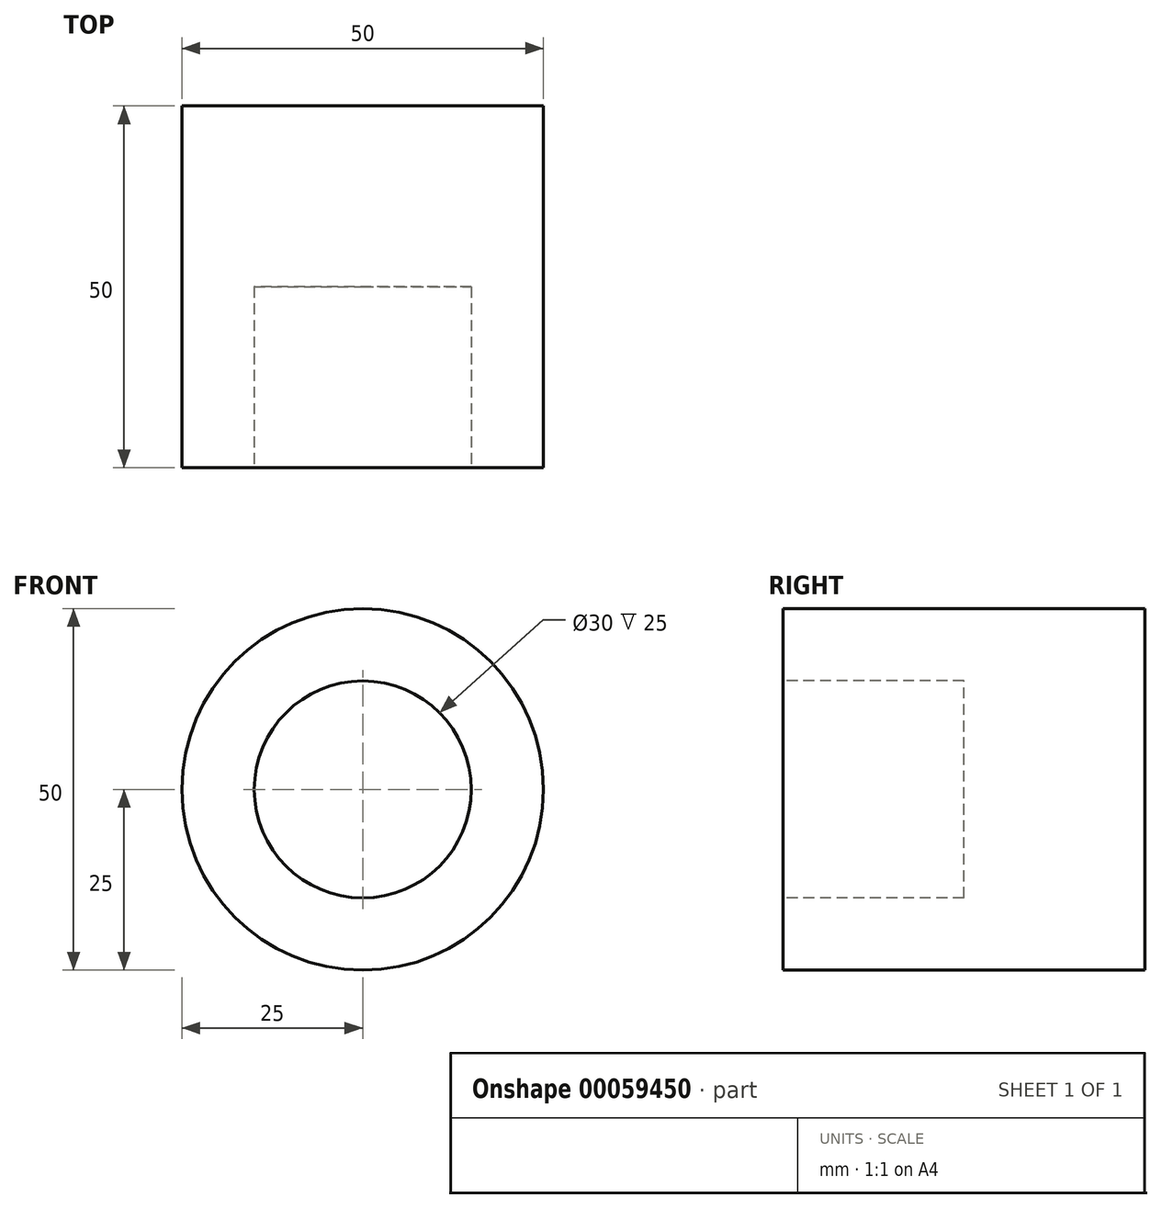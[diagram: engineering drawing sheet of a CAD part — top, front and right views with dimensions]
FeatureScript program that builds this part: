
annotation { "Feature Type Name" : "Feature", "Feature Type Description" : "" }
export const myFeature = defineFeature(function(context is Context, id is Id, definition is map)
    precondition{}
    {
        {
            var Q0;
            Q0=qCreatedBy(makeId("Front.planeOp"),FACE);
            var sketch = newSketch(context, id + "F0", { "sketchPlane" : qUnion([Q0])});
            skCircle(sketch, "E0", {"center": v(0, 0) * mm, "radius": 25 * mm});
            skSolve(sketch);
        }
        {
            var Q0;
            Q0=qSketchRegion(id+"F0",true);
            var Q1;
            Q1=sQuery(id+"F0.wireOp",EDGE,"E0");
            var Q2;
            Q2=qBodyType(qCreatedBy(id+"F0",EDGE),BodyType.WIRE);
            extrude(context, id + "F1", {"entities" : qUnion([Q0]), "surfaceEntities" : qUnion([Q1, Q2]), "oppositeDirection" : true, "depth" : 50 * mm});
        }
        {
            var Q0;
            Q0=makeQuery(id+"F1.opExtrude","CAP_FACE",FACE,{"disambiguationData":[OSD([sQuery(id+"F0.wireOp",EDGE,"E0")])],"isStart":true});
            var sketch = newSketch(context, id + "F2", { "sketchPlane" : qUnion([Q0])});
            skCircle(sketch, "E1", {"center": v(0, 0) * mm, "radius": 15 * mm});
            skSolve(sketch);
        }
        {
            var Q0;
            Q0=makeQuery(id+"F2.imprint","IMPRINT",FACE,{"disambiguationData":[TD([[makeQuery(id+"F2.imprint","IMPRINT",EDGE,{"derivedFrom":sQuery(id+"F2.wireOp",EDGE,"E1")}),1.0]])]});
            extrude(context, id + "F3", {"entities" : qUnion([Q0]), "operationType" : NewBodyOperationType.REMOVE, "oppositeDirection" : true, "depth" : 25 * mm});
        }
    });
